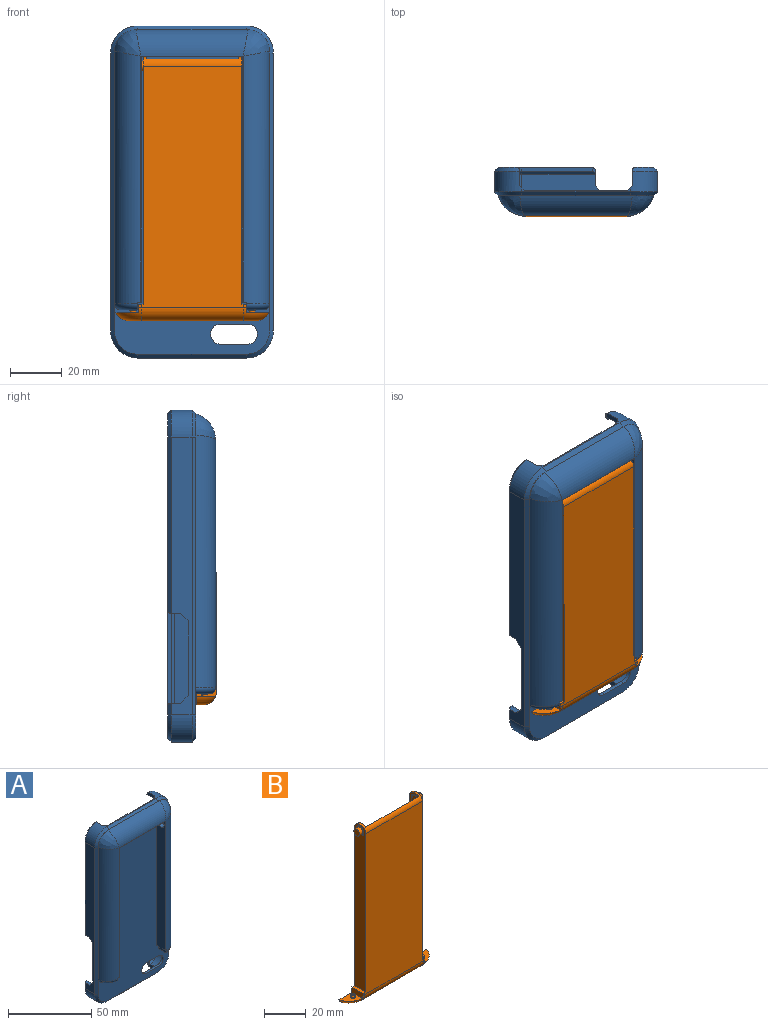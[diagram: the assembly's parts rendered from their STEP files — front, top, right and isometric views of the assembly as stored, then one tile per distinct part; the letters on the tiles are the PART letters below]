
ASSEMBLY  parts=2 mates=1
PART A: 124 faces, bbox 65x21.3x130.7 mm
  f0: plane 7.62x1.27mm, normal (0,0,-1), area 9.6mm2, adj f1,f2,f101,f104,f109
  f1: plane 95.41x39.65mm, normal (0,-1,0), area 15.3mm2, adj f0,f99,f100,f101,f102,f109,f110,f111
  f2: plane 115.83x60.51mm, normal (0,-1,0), area 4765.4mm2, adj f0,f30,f31,f32,f33,f34,f35,f37
  f3: cylinder r=8.5mm len=9.02mm, axis (0,-1,0), area 79mm2, adj f7,f25,f43,f45,f53,f80
  f4: plane 107.8x6.5mm, normal (1,0,0), area 517.2mm2, adj f5,f8,f28,f29,f49,f50,f83,f86
  f5: cylinder r=8.5mm len=9.62mm, axis (0,-1,0), area 82.6mm2, adj f4,f23,f46,f48,f52,f87
  f6: cylinder r=8.5mm len=9.62mm, axis (0,-1,0), area 82.6mm2, adj f7,f22,f44,f46,f51,f82
  f7: plane 107.8x6.5mm, normal (-1,0,0), area 700.7mm2, adj f3,f6,f42,f81
  f8: cylinder r=8.5mm len=8.5mm, axis (0,-1,0), area 86.8mm2, adj f4,f9,f47,f84
  f9: plane 30.6x6.5mm, normal (0,0,1), area 187.9mm2, adj f8,f27,f45,f54,f85
  f10: plane 36.6x12.5mm, normal (0,1,0), area 66.1mm2, adj f55,f56,f57,f66,f67,f68,f95,f98
  f11: plane 76.09x7.18mm, normal (0,1,0), area 117.5mm2, adj f63,f64,f69,f70,f90,f91,f94
  f12: plane 123.8x58.1mm, normal (0,1,0), area 7009.3mm2, adj f30,f31,f32,f33,f42,f43,f44,f45
  f13: plane 125.23x7.18mm, normal (0,1,0), area 194mm2, adj f59,f60,f61,f71,f72,f73,f92,f93
  f14: cylinder r=10.5mm len=10.5mm, axis (0,-1,0), area 126.3mm2, adj f15,f21,f22,f36,f51,f73
  f15: plane 107.8x8mm, normal (1,0,0), area 862.4mm2, adj f14,f16,f34,f72
  f16: cylinder r=10.5mm len=10.5mm, axis (0,-1,0), area 122.5mm2, adj f15,f17,f25,f35,f53,f71
  f17: plane 42.1x8mm, normal (0,0,-1), area 237.7mm2, adj f16,f18,f26,f27,f37,f53,f54,f68
  f18: cylinder r=10.5mm len=10.5mm, axis (0,-1,0), area 131.9mm2, adj f17,f19,f39,f67
  f19: plane 107.8x8mm, normal (-1,0,0), area 643.9mm2, adj f18,f20,f28,f29,f41,f50,f66,f69
  f20: cylinder r=10.5mm len=10.5mm, axis (0,-1,0), area 126.3mm2, adj f19,f21,f23,f40,f52,f70
  f21: plane 42.1x1.55mm, normal (0,0,1), area 22.2mm2, adj f14,f20,f24,f38,f51,f52
  f22: plane 6x2.01mm, normal (-1,0,0), area 11.9mm2, adj f6,f14,f51,f58,f73,f92
  f23: plane 6x2.01mm, normal (1,0,0), area 11.9mm2, adj f5,f20,f52,f65,f70,f90
  f24: plane 40x2mm, normal (0,1,0), area 80mm2, adj f21,f46,f51,f52
  f25: plane 6x2.03mm, normal (-1,0,0), area 12mm2, adj f3,f16,f53,f62,f71,f96
  f26: plane 11x2mm, normal (0,1,0), area 22mm2, adj f17,f45,f53,f54
  f27: plane 6x2mm, normal (1,0,0), area 11.9mm2, adj f9,f17,f54,f68,f77,f98
  f28: plane 4x2mm, normal (0,0,1), area 7.9mm2, adj f4,f19,f66,f79,f89,f95
  f29: plane 4x2mm, normal (0,0,-1), area 7.9mm2, adj f4,f19,f69,f74,f88,f94
  f30: cylinder r=3.88mm len=7.75mm, axis (0,-1,0), area 18.3mm2, adj f2,f12,f31,f33
  f31: plane 10.5x1.5mm, normal (0,0,1), area 15.8mm2, adj f2,f12,f30,f32
  f32: cylinder r=3.88mm len=7.75mm, axis (0,-1,0), area 18.3mm2, adj f2,f12,f31,f33
  f33: plane 10.5x1.5mm, normal (0,0,-1), area 15.8mm2, adj f2,f12,f30,f32
  f34: plane 107.8x1.5mm, normal (0.71,-0.71,0), area 228.7mm2, adj f2,f15,f35,f36,f109
  f35: cone r=10.5mm half-angle=45deg, axis (0,1,0), area 32.5mm2, adj f2,f16,f34,f37
  f36: cone r=10.5mm half-angle=45deg, axis (0,1,0), area 32.5mm2, adj f14,f34,f38,f106
  f37: plane 42.1x1.5mm, normal (0,-0.71,-0.71), area 89.3mm2, adj f2,f17,f35,f39
  f38: plane 42.1x1.5mm, normal (0,-0.71,0.71), area 89.3mm2, adj f21,f36,f40,f110
  f39: cone r=10.5mm half-angle=45deg, axis (0,1,0), area 32.5mm2, adj f2,f18,f37,f41
  f40: cone r=10.5mm half-angle=45deg, axis (0,1,0), area 32.5mm2, adj f20,f38,f41,f105
  f41: plane 107.8x1.5mm, normal (-0.71,-0.71,0), area 228.7mm2, adj f2,f19,f39,f40,f111
  f42: plane 107.8x0.5mm, normal (-0.71,0.71,0), area 76.2mm2, adj f7,f12,f43,f44
  f43: cone r=8mm half-angle=45deg, axis (0,1,0), area 9.2mm2, adj f3,f12,f42,f45
  f44: cone r=8mm half-angle=45deg, axis (0,1,0), area 9.2mm2, adj f6,f12,f42,f46
  f45: plane 42.11x0.51mm, normal (0,0.71,0.71), area 29.8mm2, adj f3,f9,f12,f26,f43,f47,f53
  f46: plane 42.14x0.54mm, normal (0,0.71,-0.71), area 29.7mm2, adj f5,f6,f12,f24,f44,f48,f51,f52
  f47: cone r=8mm half-angle=45deg, axis (0,1,0), area 9.2mm2, adj f8,f12,f45,f49
  f48: cone r=8mm half-angle=45deg, axis (0,1,0), area 9.2mm2, adj f5,f12,f46,f49
  f49: plane 107.8x0.5mm, normal (0.71,0.71,0), area 76.2mm2, adj f4,f12,f47,f48
  f50: plane 29x2mm, normal (0,1,0), area 58mm2, adj f4,f19,f88,f89
  f51: plane 2.08x2.08mm, normal (-0.71,0.71,0), area 5.7mm2, adj f6,f14,f21,f22,f24,f46
  f52: plane 2.08x2.08mm, normal (0.71,0.71,0), area 5.7mm2, adj f5,f20,f21,f23,f24,f46
  f53: plane 2.14x2.02mm, normal (-0.71,0.71,0), area 5.7mm2, adj f3,f16,f17,f25,f26,f45
  f54: plane 2x2mm, normal (0.71,0.71,0), area 5.7mm2, adj f9,f17,f26,f27
  f55: plane 27.6x1.5mm, normal (0,0,1), area 41.4mm2, adj f10,f56,f77,f85
  f56: cylinder r=7.5mm len=7.5mm, axis (0,1,0), area 17.7mm2, adj f10,f55,f57,f84
  f57: plane 3.5x1.5mm, normal (1,0,0), area 5.3mm2, adj f10,f56,f79,f83
  f58: plane 1.5x0.06mm, normal (-0.99,0,0.11), area 0.1mm2, adj f22,f76,f82,f93
  f59: cylinder r=7.5mm len=7.3mm, axis (0,1,0), area 15.1mm2, adj f13,f60,f76,f82,f93
  f60: plane 107.8x1.5mm, normal (-1,0,0), area 161.7mm2, adj f13,f59,f61,f81
  f61: cylinder r=7.5mm len=7.18mm, axis (0,1,0), area 14.3mm2, adj f13,f60,f78,f80,f97
  f62: plane 1.5x0.06mm, normal (-0.98,0,-0.18), area 0.1mm2, adj f25,f78,f80,f97
  f63: plane 67.3x1.5mm, normal (1,0,0), area 100.9mm2, adj f11,f64,f74,f86
  f64: cylinder r=7.5mm len=7.3mm, axis (0,1,0), area 15.1mm2, adj f11,f63,f75,f87,f91
  f65: plane 1.5x0.06mm, normal (0.99,0,0.11), area 0.1mm2, adj f23,f75,f87,f91
  f66: plane 4.92x1.92mm, normal (-0.71,0.71,0), area 9.2mm2, adj f10,f19,f28,f67,f95
  f67: cone r=9mm half-angle=45deg, axis (0,-1,0), area 32.5mm2, adj f10,f18,f66,f68
  f68: plane 29.02x1.92mm, normal (0,0.71,-0.71), area 60.4mm2, adj f10,f17,f27,f67,f98
  f69: plane 68.72x1.92mm, normal (-0.71,0.71,0), area 144.6mm2, adj f11,f19,f29,f70,f94
  f70: cone r=9mm half-angle=45deg, axis (0,-1,0), area 29.7mm2, adj f11,f20,f23,f69,f90
  f71: cone r=9mm half-angle=45deg, axis (0,-1,0), area 28.5mm2, adj f13,f16,f25,f72,f96
  f72: plane 107.8x1.5mm, normal (0.71,0.71,0), area 228.7mm2, adj f13,f15,f71,f73
  f73: cone r=9mm half-angle=45deg, axis (0,-1,0), area 29.7mm2, adj f13,f14,f22,f72,f92
  f74: cylinder r=1mm len=2.5mm, axis (0,-1,0), area 2.4mm2, adj f29,f63,f86,f94
  f75: cylinder r=1mm len=2.43mm, axis (0,1,0), area 2.1mm2, adj f64,f65,f87,f91
  f76: cylinder r=1mm len=2.43mm, axis (0,1,0), area 2.1mm2, adj f58,f59,f82,f93
  f77: cylinder r=1mm len=2.5mm, axis (0,-1,0), area 2.4mm2, adj f27,f55,f85,f98
  f78: cylinder r=1mm len=2.43mm, axis (0,1,0), area 2.1mm2, adj f61,f62,f80,f97
  f79: cylinder r=1mm len=2.5mm, axis (0,-1,0), area 2.4mm2, adj f28,f57,f83,f95
  f80: cone r=8.5mm half-angle=45deg, axis (0,-1,0), area 15.5mm2, adj f3,f61,f62,f78,f81
  f81: plane 107.8x1mm, normal (-0.71,-0.71,0), area 152.5mm2, adj f7,f60,f80,f82
  f82: cone r=8.5mm half-angle=45deg, axis (0,-1,0), area 16.3mm2, adj f6,f58,f59,f76,f81
  f83: plane 4.92x1.42mm, normal (0.71,-0.71,0), area 6.1mm2, adj f4,f57,f79,f84
  f84: cone r=8.5mm half-angle=45deg, axis (0,-1,0), area 17.8mm2, adj f8,f56,f83,f85
  f85: plane 29.02x1.42mm, normal (0,-0.71,0.71), area 40.1mm2, adj f9,f55,f77,f84
  f86: plane 68.72x1.42mm, normal (0.71,-0.71,0), area 96.3mm2, adj f4,f63,f74,f87
  f87: cone r=8.5mm half-angle=45deg, axis (0,-1,0), area 16.3mm2, adj f5,f64,f65,f75,f86
  f88: plane 3x3mm, normal (0,0.71,-0.71), area 8.5mm2, adj f4,f19,f29,f50
  f89: plane 3x3mm, normal (0,0.71,0.71), area 8.5mm2, adj f4,f19,f28,f50
  f90: cylinder r=1mm len=1.56mm, axis (0,0,-1), area 1.5mm2, adj f11,f23,f70,f91
  f91: cylinder r=1mm len=1.23mm, axis (0.11,0,-0.99), area 1.1mm2, adj f11,f64,f65,f75,f90
  f92: cylinder r=1mm len=1.56mm, axis (0,0,-1), area 1.5mm2, adj f13,f22,f73,f93
  f93: cylinder r=1mm len=1.23mm, axis (0.11,0,0.99), area 1.1mm2, adj f13,f58,f59,f76,f92
  f94: cylinder r=1mm len=2.5mm, axis (1,0,0), area 2.4mm2, adj f11,f29,f69,f74
  f95: cylinder r=1mm len=2.5mm, axis (1,0,0), area 2.4mm2, adj f10,f28,f66,f79
  f96: cylinder r=1mm len=1.61mm, axis (0,0,1), area 1.5mm2, adj f13,f25,f71,f97
  f97: cylinder r=1mm len=1.31mm, axis (-0.18,0,0.98), area 1.2mm2, adj f13,f61,f62,f78,f96
  f98: cylinder r=1mm len=2.5mm, axis (0,0,1), area 2.4mm2, adj f10,f27,f68,f77
  f99: plane 7.62x1.27mm, normal (0,0,-1), area 9.6mm2, adj f1,f2,f100,f103,f111
  f100: plane 95.25x7.62mm, normal (1,0,0), area 705.5mm2, adj f1,f2,f99,f102,f116
  f101: plane 95.25x7.62mm, normal (-1,0,0), area 705.5mm2, adj f0,f1,f2,f102,f114
  f102: plane 39.56x7.62mm, normal (0,0,-1), area 301.4mm2, adj f1,f2,f100,f101
  f103: plane 7.71x3.14mm, normal (1,0,0), area 21.4mm2, adj f2,f99,f107,f111,f123
  f104: plane 7.71x3.14mm, normal (-1,0,0), area 21.4mm2, adj f0,f2,f108,f109,f122
  f105: plane 10.89x10.89mm, normal (0,1,0), area 2.7mm2, adj f40,f110,f111,f113
  f106: plane 10.89x10.89mm, normal (0,1,0), area 2.7mm2, adj f36,f109,f110,f112
  f107: plane 6.59x5.24mm, normal (0,0,-1), area 13.8mm2, adj f2,f103,f120,f123
  f108: plane 6.59x5.24mm, normal (0,0,-1), area 13.8mm2, adj f2,f104,f118,f122
  f109: cylinder r=10.67mm len=98.06mm, axis (0,0,-1), area 1325.9mm2, adj f0,f1,f34,f104,f106,f112,f122
  f110: cylinder r=10.67mm len=43.55mm, axis (1,0,0), area 568.5mm2, adj f1,f38,f105,f106,f112,f113
  f111: cylinder r=10.67mm len=98.06mm, axis (0,0,-1), area 1325.9mm2, adj f1,f41,f99,f103,f105,f113,f123
  f112: bspline ~10.53x10.53mm, area 67.1mm2, adj f106,f109,f110
  f113: bspline ~10.53x10.53mm, area 67.1mm2, adj f105,f110,f111
  f114: cylinder r=2.54mm len=5.08mm, axis (-1,0,0), area 50.7mm2, adj f101,f115
  f115: plane 5.08x5.08mm, normal (-1,0,0), area 20.3mm2, adj f114
  f116: cylinder r=2.54mm len=5.08mm, axis (1,0,0), area 50.7mm2, adj f100,f117
  f117: plane 5.08x5.08mm, normal (1,0,0), area 20.3mm2, adj f116
  f118: cylinder r=1.91mm len=3.81mm, axis (0,0,-1), area 30.4mm2, adj f108,f119,f122
  f119: plane 3.81x3.81mm, normal (0,0,-1), area 11.4mm2, adj f118
  f120: cylinder r=1.91mm len=3.81mm, axis (0,0,-1), area 30.4mm2, adj f107,f121,f123
  f121: plane 3.81x3.81mm, normal (0,0,-1), area 11.4mm2, adj f120
  f122: torus R=8.38mm, axis (0,0,1), area 37.8mm2, adj f2,f104,f108,f109,f118
  f123: torus R=8.38mm, axis (0,0,1), area 37.8mm2, adj f2,f103,f107,f111,f120
PART B: 60 faces, bbox 62.7x10.9x103.2 mm
  f0: torus R=5.59mm, axis (0,0,1), area 59.3mm2, adj f1,f3,f9,f10,f15,f17,f58
  f1: cylinder r=5.08mm len=39.65mm, axis (-1,0,0), area 310.5mm2, adj f0,f2,f14,f58
  f2: torus R=5.59mm, axis (0,0,1), area 61.2mm2, adj f1,f4,f12,f13,f15,f16,f58
  f3: plane 2.81x1.73mm, normal (0,0,-1), area 0.2mm2, adj f0,f58
  f4: plane 2.69x1.38mm, normal (0,0,-1), area 0.2mm2, adj f2,f58
  f5: plane 1.27x0.75mm, normal (0,0,1), area 1mm2, adj f18,f25,f56,f57
  f6: plane 3.81x1.91mm, normal (-1,0,0), area 0mm2, adj f23,f44
  f7: plane 3.81x1.91mm, normal (1,0,0), area 0mm2, adj f21,f33
  f8: plane 7.62x1.78mm, normal (0,0,1), area 13.5mm2, adj f10,f14,f15,f17,f19
  f9: plane 8.76x7.19mm, normal (0,0,1), area 39.5mm2, adj f0,f10,f15,f49
  f10: plane 7.58x3.19mm, normal (1,0,0), area 23.8mm2, adj f0,f8,f9,f15,f17
  f11: plane 7.62x1.78mm, normal (0,0,1), area 13.5mm2, adj f12,f14,f15,f16,f18
  f12: plane 7.58x3.19mm, normal (-1,0,0), area 23.8mm2, adj f2,f11,f13,f15,f16
  f13: plane 8.76x7.19mm, normal (0,0,1), area 39.5mm2, adj f2,f12,f15,f51
  f14: plane 93.72x39.65mm, normal (0,-1,0), area 3586.8mm2, adj f1,f8,f11,f16,f17,f18,f19,f56
  f15: plane 99.79x60.31mm, normal (0,1,0), area 344.6mm2, adj f0,f2,f8,f9,f10,f11,f12,f13
  f16: cylinder r=10.67mm len=1.27mm, axis (0,0,1), area 1.4mm2, adj f2,f11,f12,f14
  f17: cylinder r=10.67mm len=1.27mm, axis (0,0,1), area 1.4mm2, adj f0,f8,f10,f14
  f18: plane 95.89x7.62mm, normal (-1,0,0), area 708.1mm2, adj f5,f11,f14,f15,f23,f39,f40,f41
  f19: plane 95.89x7.62mm, normal (1,0,0), area 708.1mm2, adj f8,f14,f15,f20,f21,f29,f30,f31
  f20: plane 1.27x0.75mm, normal (0,0,1), area 1mm2, adj f19,f27,f55,f56
  f21: cylinder r=1.91mm len=3.81mm, axis (-1,0,0), area 27.4mm2, adj f7,f19,f22,f27,f33,f34
  f22: plane 3.81x3.81mm, normal (1,0,0), area 11.4mm2, adj f21
  f23: cylinder r=1.91mm len=3.81mm, axis (1,0,0), area 27.4mm2, adj f6,f18,f24,f25,f43,f44
  f24: plane 3.81x3.81mm, normal (-1,0,0), area 11.4mm2, adj f23
  f25: plane 98.04x6.35mm, normal (1,0,0), area 613.5mm2, adj f5,f15,f23,f26,f28,f39,f40,f41
  f26: plane 97.28x35.71mm, normal (0,1,0), area 3474mm2, adj f25,f27,f28,f56
  f27: plane 98.04x6.35mm, normal (-1,0,0), area 613.5mm2, adj f15,f20,f21,f26,f28,f29,f30,f31
  f28: plane 35.71x6.35mm, normal (0,0,1), area 226.8mm2, adj f15,f25,f26,f27
  f29: plane 2.4x1.27mm, normal (0,-1,0), area 3mm2, adj f19,f27,f30,f38
  f30: plane 1.27x0.47mm, normal (0,0,1), area 0.6mm2, adj f19,f27,f29,f31
  f31: plane 1.27x0.95mm, normal (0,1,0), area 1.2mm2, adj f19,f27,f30,f32
  f32: plane 1.44x1.27mm, normal (0,1,0.07), area 1.8mm2, adj f19,f27,f31,f33
  f33: cylinder r=1.91mm len=3.81mm, axis (1,0,0), area 7.6mm2, adj f7,f21,f27,f32
  f34: plane 1.57x1.27mm, normal (0,-1,0), area 2mm2, adj f19,f21,f27,f35
  f35: plane 1.27x0.21mm, normal (0,-1,0), area 0.3mm2, adj f19,f27,f34,f36
  f36: plane 1.27x0.57mm, normal (0,0,1), area 0.7mm2, adj f19,f27,f35,f37
  f37: plane 1.78x1.27mm, normal (0,1,0), area 2.3mm2, adj f19,f27,f36,f38
  f38: cylinder r=2.47mm len=4.94mm, axis (1,0,0), area 9.9mm2, adj f19,f27,f29,f37
  f39: cylinder r=2.47mm len=4.94mm, axis (1,0,0), area 9.9mm2, adj f18,f25,f40,f48
  f40: plane 1.78x1.27mm, normal (0,1,0), area 2.3mm2, adj f18,f25,f39,f41
  f41: plane 1.27x0.57mm, normal (0,0,1), area 0.7mm2, adj f18,f25,f40,f42
  f42: plane 1.27x0.21mm, normal (0,-1,0), area 0.3mm2, adj f18,f25,f41,f43
  f43: plane 1.57x1.27mm, normal (0,-1,0), area 2mm2, adj f18,f23,f25,f42
  f44: cylinder r=1.91mm len=3.81mm, axis (1,0,0), area 7.6mm2, adj f6,f23,f25,f45
  f45: plane 1.44x1.27mm, normal (0,1,0.07), area 1.8mm2, adj f18,f25,f44,f46
  f46: plane 1.27x0.95mm, normal (0,1,0), area 1.2mm2, adj f18,f25,f45,f47
  f47: plane 1.27x0.47mm, normal (0,0,1), area 0.6mm2, adj f18,f25,f46,f48
  f48: plane 2.4x1.27mm, normal (0,-1,0), area 3mm2, adj f18,f25,f39,f47
  f49: cylinder r=1.27mm len=2.54mm, axis (0,0,-1), area 5.1mm2, adj f9,f54
  f50: plane 1.27x1.27mm, normal (0,0,1), area 1.3mm2, adj f54
  f51: cylinder r=1.27mm len=2.54mm, axis (0,0,-1), area 5.1mm2, adj f13,f53
  f52: plane 1.27x1.27mm, normal (0,0,1), area 1.3mm2, adj f53
  f53: torus R=0.64mm, axis (0,0,1), area 6.5mm2, adj f51,f52
  f54: torus R=0.64mm, axis (0,0,1), area 6.5mm2, adj f49,f50
  f55: cylinder r=3.43mm len=3.43mm, axis (-1,0,0), area 6.9mm2, adj f15,f19,f20,f27
  f56: cylinder r=3.43mm len=38.25mm, axis (1,0,0), area 122.7mm2, adj f5,f14,f18,f19,f20,f25,f26,f27
  f57: cylinder r=3.43mm len=3.43mm, axis (-1,0,0), area 6.9mm2, adj f5,f15,f18,f25
  f58: extruded ~49.27x2.82mm, area 129.8mm2, adj f0,f1,f2,f3,f4,f15,f59
  f59: plane 49.27x3.22mm, normal (0,0,-1), area 123.5mm2, adj f15,f58
PLACE A t=(-52.78,-72.17,-4.11)mm
PLACE B rot(axis=(-1,0,0),0.2deg) t=(-65.35,-72.52,-54.09)mm
MATE cylindrical B.f23 <-> A.f116  axis (-1,0,0) through (-74.03,-75.98,44.73)mm
